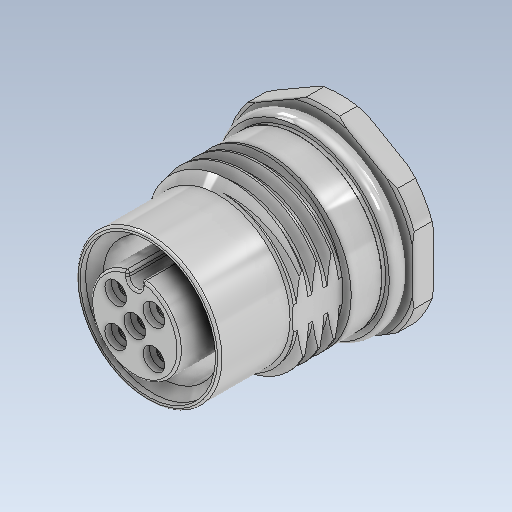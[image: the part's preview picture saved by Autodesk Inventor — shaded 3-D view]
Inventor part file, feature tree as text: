
AUTODESK INVENTOR PART (.ipt)
format: ipt  version: 2021 (Build 250183000, 183)  size: 755,200 bytes
history: native  units: mm
features: sketch x2, extrude x1, imported_body x1
ambient origin geometry x8: Origin, YZ Plane, XZ Plane, XY Plane, X Axis, Y Axis, Z Axis, Center Point
bodies: Solid1 (feature_tree)
feature tree (4):
  sketch  "Sketch1"  dims[d0=0.0mm d1=0.0mm]
  extrude  "Extrusion1"  [1 undecoded]
  sketch  "Sketch2"
  imported_body  "Base1"
note: 1 required parameter value undecoded (feature->parameter linkage not recoverable at this tier; creation-order binding heuristic only, values carry confidence <= 0.55)
